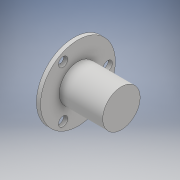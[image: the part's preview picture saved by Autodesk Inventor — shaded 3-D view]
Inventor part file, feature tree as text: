
AUTODESK INVENTOR PART (.ipt)
format: ipt  version: 2017 (Build 210142000, 142)  size: 126,976 bytes
history: native  units: mm
features: extrude x4, sketch x4
ambient origin geometry x8: Origin, YZ Plane, XZ Plane, XY Plane, X Axis, Y Axis, Z Axis, Center Point
bodies: Solid1 (feature_tree)
feature tree (8):
  extrude  "Extrusion1"  Depth=2.4mm TaperAngle=0.0deg
  extrude  "Extrusion2"  Depth=5.5mm
  extrude  "Extrusion3"  Depth=2.4mm TaperAngle=0.0deg
  extrude  "Extrusion4"  Depth=25.6mm TaperAngle=0.0deg
  sketch  "Sketch1"  dims[d0=44.0mm d1=2.4mm d2=0.0mm]
  sketch  "Sketch2"  dims[d3=17.5mm d4=5.5mm]
  sketch  "Sketch3"  dims[d5=30.0mm d7=360.0deg d9=2.4mm d10=0.0mm]
  sketch  "Sketch4"  dims[d11=22.0mm d12=25.6mm d13=0.0mm d14=7.8mm d15=9.0mm d16=0.0mm]
